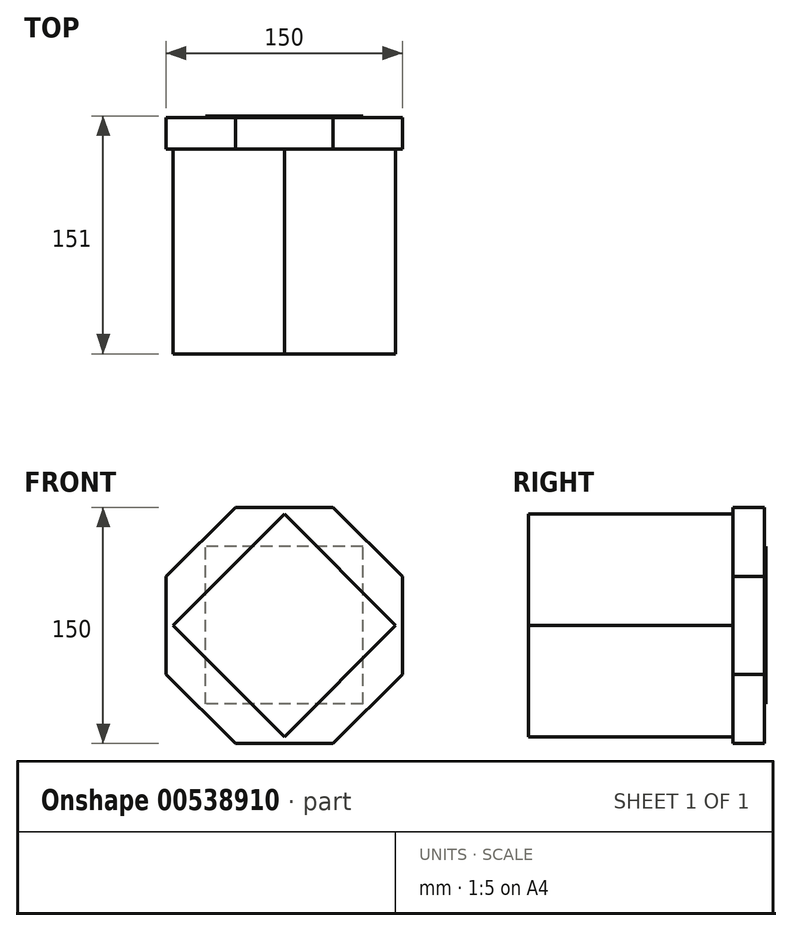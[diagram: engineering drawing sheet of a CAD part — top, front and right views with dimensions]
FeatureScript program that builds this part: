
annotation { "Feature Type Name" : "Feature", "Feature Type Description" : "" }
export const myFeature = defineFeature(function(context is Context, id is Id, definition is map)
    precondition{}
    {
        {
            var Q0;
            Q0=qCreatedBy(makeId("Front.planeOp"),FACE);
            var sketch = newSketch(context, id + "F0", { "sketchPlane" : qUnion([Q0])});
            skCircle(sketch, "E0.cCircle", {"center": v(0, 0) * mm, "radius": 75 * mm, "construction": true});
            skLineSegment(sketch, "E0.0", {"start": v(31.07, -75) * mm, "end": v(-31.07, -75) * mm});
            skLineSegment(sketch, "E0.1", {"start": v(-31.07, -75) * mm, "end": v(-75, -31.07) * mm});
            skLineSegment(sketch, "E0.2", {"start": v(-75, -31.07) * mm, "end": v(-75, 31.07) * mm});
            skLineSegment(sketch, "E0.3", {"start": v(-75, 31.07) * mm, "end": v(-31.07, 75) * mm});
            skLineSegment(sketch, "E0.4", {"start": v(-31.07, 75) * mm, "end": v(31.07, 75) * mm});
            skLineSegment(sketch, "E0.5", {"start": v(31.07, 75) * mm, "end": v(75, 31.07) * mm});
            skLineSegment(sketch, "E0.6", {"start": v(75, 31.07) * mm, "end": v(75, -31.07) * mm});
            skLineSegment(sketch, "E0.7", {"start": v(75, -31.07) * mm, "end": v(31.07, -75) * mm});
            skPoint(sketch, "E0.0.midPoint", {"position": v(0, -75) * mm});
            skLineSegment(sketch, "E1", {"start": v(-53.03, 53.03) * mm, "end": v(54.3, 51.76) * mm});
            skLineSegment(sketch, "E2", {"start": v(-53.03, -53.03) * mm, "end": v(53.03, -53.03) * mm});
            skLineSegment(sketch, "E3", {"start": v(-53.03, -53.03) * mm, "end": v(-53.03, 53.03) * mm});
            skLineSegment(sketch, "E4", {"start": v(53.03, -53.03) * mm, "end": v(54.3, 51.76) * mm});
            skSolve(sketch);
        }
        {
            var Q0;
            Q0 = qSketchRegion(id + "F0", true);
            extrude(context, id + "F1", {"entities" : qUnion([Q0]), "oppositeDirection" : true, "depth" : 20 * mm, "offsetDistance" : 25 * mm});
        }
        {
            var Q0;
            Q0=makeQuery(id+"F1.opExtrude","CAP_FACE",FACE,{"disambiguationData":[OSD([sQuery(id+"F0.wireOp",EDGE,"E0.0"),sQuery(id+"F0.wireOp",EDGE,"E0.1"),sQuery(id+"F0.wireOp",EDGE,"E0.2"),sQuery(id+"F0.wireOp",EDGE,"E0.3"),sQuery(id+"F0.wireOp",EDGE,"E0.4"),sQuery(id+"F0.wireOp",EDGE,"E0.5"),sQuery(id+"F0.wireOp",EDGE,"E0.6"),sQuery(id+"F0.wireOp",EDGE,"E0.7")])],"isStart":true});
            var sketch = newSketch(context, id + "F2", { "sketchPlane" : qUnion([Q0])});
            skLineSegment(sketch, "E5.bottom", {"start": v(50, -50) * mm, "end": v(-50, -50) * mm});
            skLineSegment(sketch, "E5.top", {"start": v(50, 50) * mm, "end": v(-50, 50) * mm});
            skLineSegment(sketch, "E5.left", {"start": v(50, -50) * mm, "end": v(50, 50) * mm});
            skLineSegment(sketch, "E5.right", {"start": v(-50, -50) * mm, "end": v(-50, 50) * mm});
            skPoint(sketch, "E5.middle", {"position": v(0, 0) * mm});
            skSolve(sketch);
        }
        {
            var Q0;
            Q0=makeQuery(id+"F2.imprint","IMPRINT",FACE,{"disambiguationData":[TD([[makeQuery(id+"F2.imprint","IMPRINT",EDGE,{"derivedFrom":sQuery(id+"F2.wireOp",EDGE,"E5.bottom")}),-1.0]])]});
            extrude(context, id + "F3", {"entities" : qUnion([Q0]), "operationType" : NewBodyOperationType.ADD, "oppositeDirection" : true, "depth" : 21 * mm, "offsetDistance" : 25 * mm});
        }
        {
            var Q0;
            Q0=makeQuery(id+"F1.opExtrude","CAP_FACE",FACE,{"disambiguationData":[OSD([sQuery(id+"F0.wireOp",EDGE,"E0.0"),sQuery(id+"F0.wireOp",EDGE,"E0.1"),sQuery(id+"F0.wireOp",EDGE,"E0.2"),sQuery(id+"F0.wireOp",EDGE,"E0.3"),sQuery(id+"F0.wireOp",EDGE,"E0.4"),sQuery(id+"F0.wireOp",EDGE,"E0.5"),sQuery(id+"F0.wireOp",EDGE,"E0.6"),sQuery(id+"F0.wireOp",EDGE,"E0.7")])],"isStart":true});
            var sketch = newSketch(context, id + "F4", { "sketchPlane" : qUnion([Q0])});
            skLineSegment(sketch, "E6", {"start": v(0, 0) * mm, "end": v(35.36, 35.36) * mm, "construction": true});
            skLineSegment(sketch, "E7", {"start": v(0, 0) * mm, "end": v(-35.36, -35.36) * mm, "construction": true});
            skLineSegment(sketch, "E8", {"start": v(0, 0) * mm, "end": v(35.36, -35.36) * mm, "construction": true});
            skLineSegment(sketch, "E9", {"start": v(0, 0) * mm, "end": v(-35.36, 35.36) * mm, "construction": true});
            skLineSegment(sketch, "E10", {"start": v(-35.36, 35.36) * mm, "end": v(0, 70.71) * mm});
            skLineSegment(sketch, "E11", {"start": v(0, 70.71) * mm, "end": v(70.71, 0) * mm});
            skPoint(sketch, "E11.endSnap0", {"position": v(75, 0) * mm});
            skLineSegment(sketch, "E12", {"start": v(70.71, 0) * mm, "end": v(0, -70.71) * mm});
            skLineSegment(sketch, "E13", {"start": v(0, -70.71) * mm, "end": v(-70.71, 0) * mm});
            skLineSegment(sketch, "E14", {"start": v(-70.71, 0) * mm, "end": v(-35.36, 35.36) * mm});
            skSolve(sketch);
        }
        {
            var Q0;
            Q0=makeQuery(id+"F4.imprint","IMPRINT",FACE,{"disambiguationData":[TD([[makeQuery(id+"F4.imprint","IMPRINT",EDGE,{"derivedFrom":sQuery(id+"F4.wireOp",EDGE,"E10")}),-1.0]])]});
            extrude(context, id + "F5", {"entities" : qUnion([Q0]), "operationType" : NewBodyOperationType.ADD, "depth" : 130 * mm, "offsetDistance" : 25 * mm});
        }
    });
